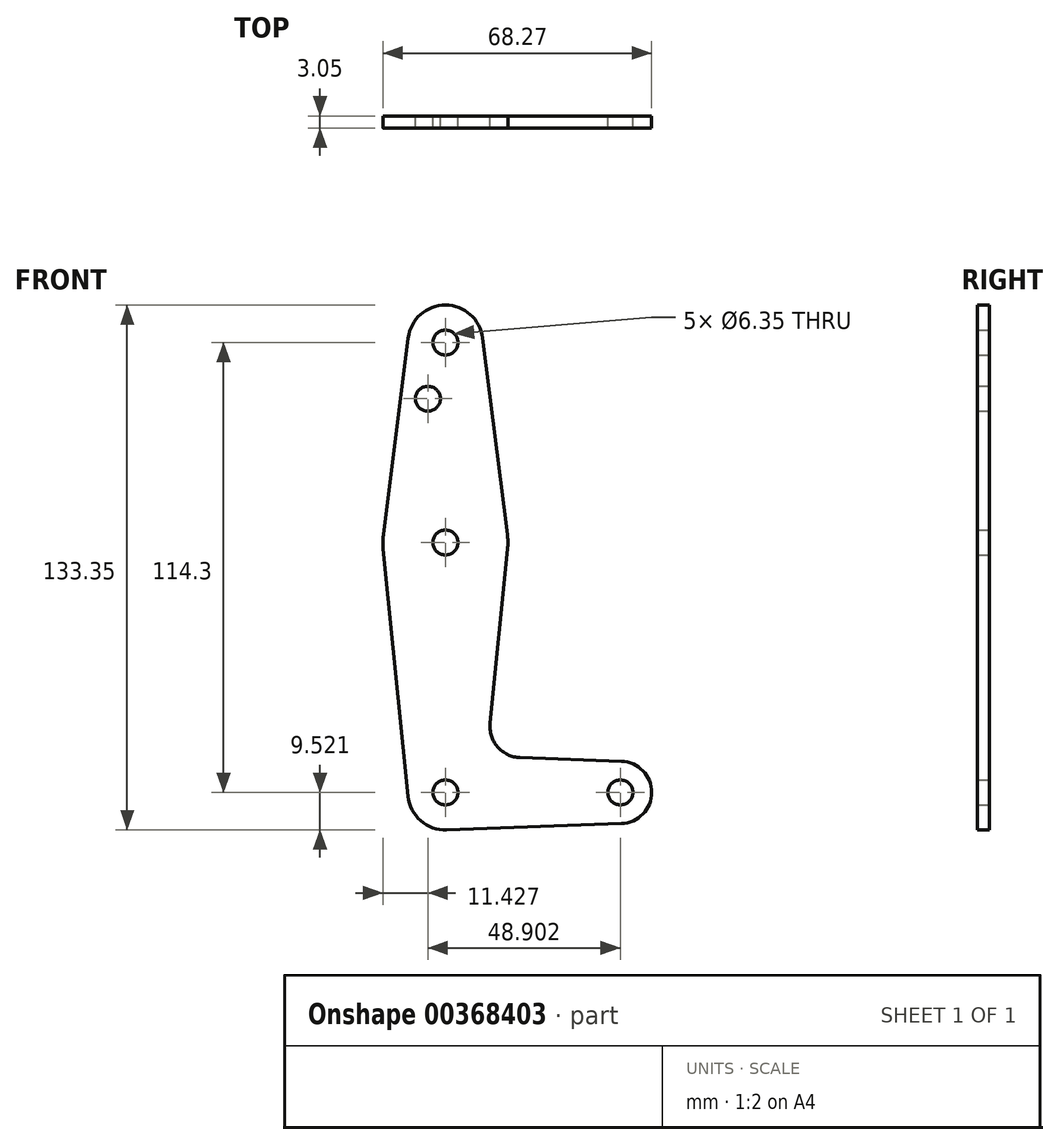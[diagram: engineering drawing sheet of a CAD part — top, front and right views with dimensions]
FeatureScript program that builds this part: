
annotation { "Feature Type Name" : "Feature", "Feature Type Description" : "" }
export const myFeature = defineFeature(function(context is Context, id is Id, definition is map)
    precondition{}
    {
        {
            var Q0;
            Q0=qCreatedBy(makeId("Front.planeOp"),FACE);
            var sketch = newSketch(context, id + "F0", { "sketchPlane" : qUnion([Q0])});
            skLineSegment(sketch, "E0", {"start": v(-32.5, 61.98) * mm, "end": v(-32.5, -52.32) * mm});
            skLineSegment(sketch, "E1", {"start": v(-32.5, -52.32) * mm, "end": v(11.95, -52.32) * mm});
            skCircle(sketch, "E2", {"center": v(-32.5, 61.98) * mm, "radius": 9.53 * mm});
            skCircle(sketch, "E3", {"center": v(-32.5, -52.32) * mm, "radius": 9.53 * mm});
            skCircle(sketch, "E4", {"center": v(-32.5, 11.18) * mm, "radius": 15.88 * mm});
            skCircle(sketch, "E5", {"center": v(11.95, -52.32) * mm, "radius": 7.94 * mm});
            skLineSegment(sketch, "E6", {"start": v(-23.05, 63.17) * mm, "end": v(-16.75, 13.17) * mm});
            skLineSegment(sketch, "E7", {"start": v(-13.53, -43.47) * mm, "end": v(12.23, -44.39) * mm});
            skLineSegment(sketch, "E8", {"start": v(-41.95, 63.17) * mm, "end": v(-48.25, 13.17) * mm});
            skLineSegment(sketch, "E9", {"start": v(-16.7, 9.6) * mm, "end": v(-21.16, -34.73) * mm});
            skCircle(sketch, "E10", {"center": v(-32.5, -52.32) * mm, "radius": 3.18 * mm});
            skCircle(sketch, "E11", {"center": v(11.95, -52.32) * mm, "radius": 3.18 * mm});
            skCircle(sketch, "E12", {"center": v(-32.5, 11.18) * mm, "radius": 3.18 * mm});
            skCircle(sketch, "E13", {"center": v(-32.5, 61.98) * mm, "radius": 3.18 * mm});
            skCircle(sketch, "E14", {"center": v(-36.95, 47.7) * mm, "radius": 3.18 * mm});
            skArc(sketch, "E15.filletArc", {"start": v(-21.16, -34.73) * mm, "mid": v(-19.24, -40.75) * mm, "end": v(-13.53, -43.47) * mm});
            skLineSegment(sketch, "E16", {"start": v(-48.3, 9.6) * mm, "end": v(-41.98, -53.27) * mm});
            skLineSegment(sketch, "E17", {"start": v(-32.16, -61.84) * mm, "end": v(12.23, -60.25) * mm});
            skSolve(sketch);
        }
        {
            var Q0;
            Q0 = qSketchRegion(id + "F0", true);
            var Q1;
            {var subQ0=sQuery(id+"F0.wireOp",EDGE,"E3");var subQ1=sQuery(id+"F0.wireOp",EDGE,"E0");var subQ2=makeQuery(id+"F0.imprint","INTERSECT",VERTEX,{"derivedFrom":[subQ1,subQ0]});Q1=makeQuery(id+"F0.imprint","IMPRINT",FACE,{"disambiguationData":[TD([[makeQuery(id+"F0.imprint","IMPRINT",EDGE,{"disambiguationData":[TD([[subQ2,-1.0]])],"derivedFrom":subQ1}),1.0]])]});}
            var Q2;
            Q2 = qConstructionFilter(qBodyType(qCreatedBy(id + "F0" ,EDGE), BodyType.WIRE), ConstructionObject.NO);
            extrude(context, id + "F1", {"entities" : qUnion([Q0, Q1]), "surfaceEntities" : qUnion([Q2]), "depth" : 3.05 * mm});
        }
    });
